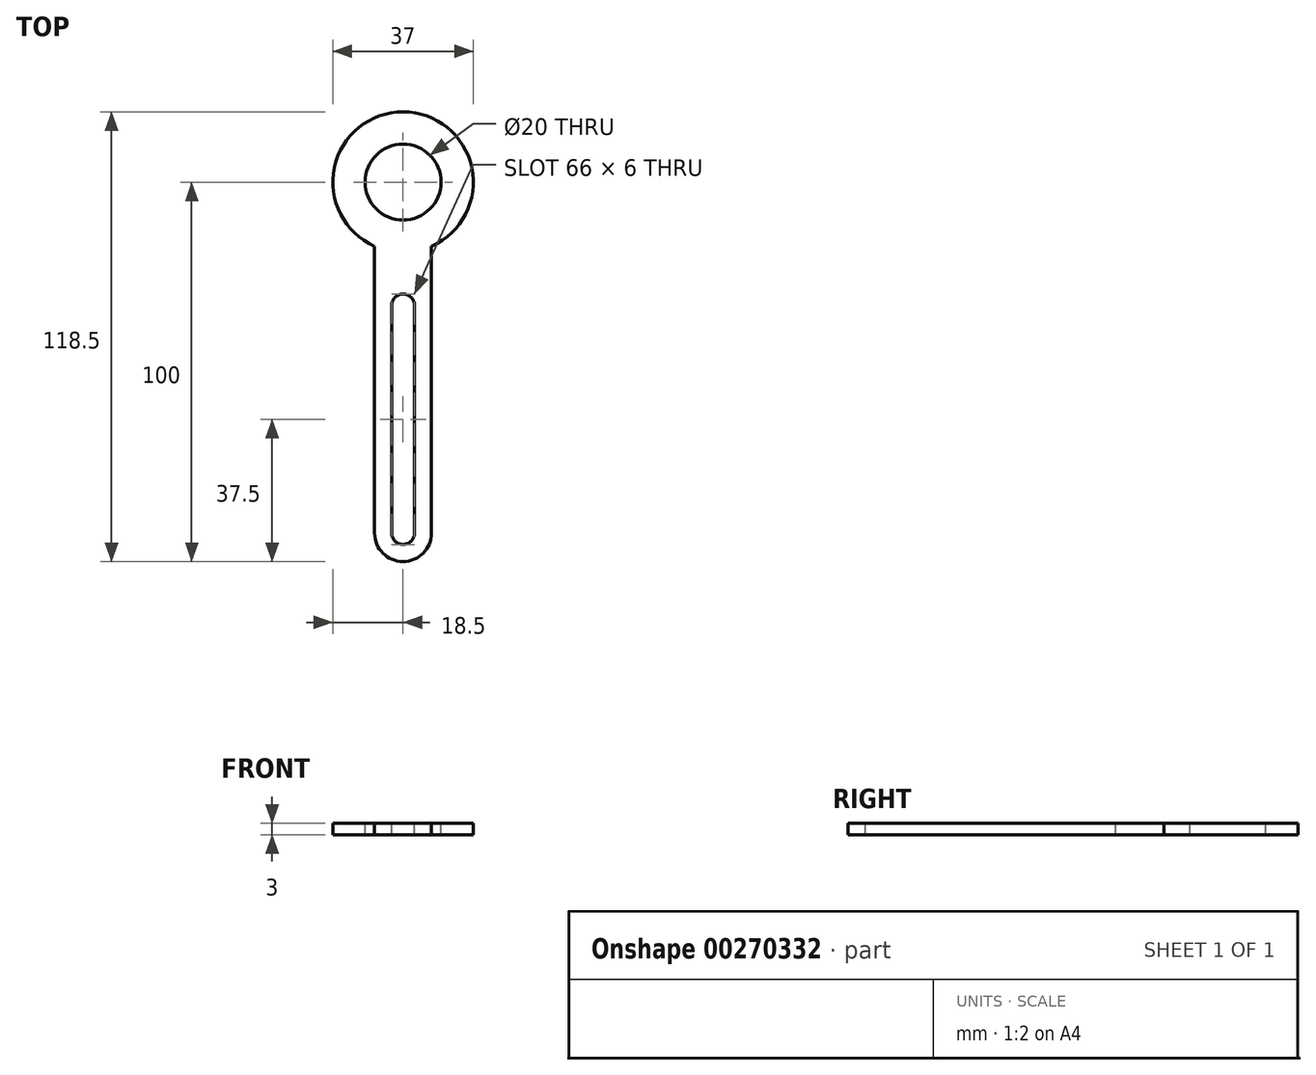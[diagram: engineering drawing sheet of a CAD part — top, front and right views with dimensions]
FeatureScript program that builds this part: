
annotation { "Feature Type Name" : "Feature", "Feature Type Description" : "" }
export const myFeature = defineFeature(function(context is Context, id is Id, definition is map)
    precondition{}
    {
        {
            var Q0;
            Q0=qCreatedBy(makeId("Top.planeOp"),FACE);
            var sketch = newSketch(context, id + "F0", { "sketchPlane" : qUnion([Q0])});
            skCircle(sketch, "E0", {"center": v(0, 0) * mm, "radius": 18.5 * mm});
            skLineSegment(sketch, "E1.bottom", {"start": v(7.5, -100) * mm, "end": v(-7.5, -100) * mm});
            skLineSegment(sketch, "E1.top", {"start": v(7.5, 100) * mm, "end": v(-7.5, 100) * mm});
            skLineSegment(sketch, "E1.left", {"start": v(7.5, -100) * mm, "end": v(7.5, 100) * mm});
            skLineSegment(sketch, "E1.right", {"start": v(-7.5, -100) * mm, "end": v(-7.5, 100) * mm});
            skSolve(sketch);
        }
        {
            var Q0;
            {var subQ0=sQuery(id+"F0.wireOp",EDGE,"E1.right");var subQ1=sQuery(id+"F0.wireOp",EDGE,"E0");var subQ2=makeQuery(id+"F0.imprint","INTERSECT",VERTEX,{"disambiguationData":[OD(0.0)],"derivedFrom":[subQ1,subQ0]});Q0=makeQuery(id+"F0.imprint","IMPRINT",FACE,{"disambiguationData":[TD([[makeQuery(id+"F0.imprint","IMPRINT",EDGE,{"disambiguationData":[TD([[subQ2,1.0]])],"derivedFrom":subQ1}),1.0]])]});}
            var Q1;
            {var subQ0=sQuery(id+"F0.wireOp",EDGE,"E1.right");var subQ1=sQuery(id+"F0.wireOp",EDGE,"E0");var subQ2=makeQuery(id+"F0.imprint","INTERSECT",VERTEX,{"disambiguationData":[OD(0.0)],"derivedFrom":[subQ1,subQ0]});Q1=makeQuery(id+"F0.imprint","IMPRINT",FACE,{"disambiguationData":[TD([[makeQuery(id+"F0.imprint","IMPRINT",EDGE,{"disambiguationData":[TD([[subQ2,-1.0]])],"derivedFrom":subQ1}),1.0]])]});}
            var Q2;
            {var subQ0=sQuery(id+"F0.wireOp",EDGE,"E1.left");var subQ1=sQuery(id+"F0.wireOp",EDGE,"E0");var subQ2=makeQuery(id+"F0.imprint","INTERSECT",VERTEX,{"disambiguationData":[OD(0.0)],"derivedFrom":[subQ1,subQ0]});Q2=makeQuery(id+"F0.imprint","IMPRINT",FACE,{"disambiguationData":[TD([[makeQuery(id+"F0.imprint","IMPRINT",EDGE,{"disambiguationData":[TD([[subQ2,1.0]])],"derivedFrom":subQ1}),1.0]])]});}
            var Q3;
            {var subQ5=sQuery(id+"F0.wireOp",EDGE,"E1.bottom");Q3=makeQuery(id+"F0.imprint","IMPRINT",FACE,{"disambiguationData":[TD([[makeQuery(id+"F0.imprint","IMPRINT",EDGE,{"derivedFrom":subQ5}),-1.0]])]});}
            extrude(context, id + "F1", {"entities" : qUnion([Q0, Q1, Q2, Q3]), "depth" : 3 * mm});
        }
        {
            var Q0;
            Q0=makeQuery(id+"F1.opExtrude","CAP_FACE",FACE,{"disambiguationData":[OSD([sQuery(id+"F0.wireOp",EDGE,"E0"),sQuery(id+"F0.wireOp",EDGE,"E1.bottom"),sQuery(id+"F0.wireOp",EDGE,"E1.left"),sQuery(id+"F0.wireOp",EDGE,"E1.right")])],"isStart":false});
            var sketch = newSketch(context, id + "F2", { "sketchPlane" : qUnion([Q0])});
            skCircle(sketch, "E2", {"center": v(0, 0) * mm, "radius": 10 * mm});
            skSolve(sketch);
        }
        {
            var Q0;
            Q0 = qSketchRegion(id + "F2", true);
            extrude(context, id + "F3", {"entities" : qUnion([Q0]), "operationType" : NewBodyOperationType.REMOVE, "oppositeDirection" : true, "depth" : 25 * mm});
        }
        {
            var Q0;
            Q0=makeQuery(id+"F1.opExtrude","SWEPT_EDGE",EDGE,{"disambiguationData":[OSD([sQuery(id+"F0.wireOp",EDGE,"E1.bottom"),sQuery(id+"F0.wireOp",EDGE,"E1.left")])]});
            var Q1;
            Q1=makeQuery(id+"F1.opExtrude","SWEPT_EDGE",EDGE,{"disambiguationData":[OSD([sQuery(id+"F0.wireOp",EDGE,"E1.bottom"),sQuery(id+"F0.wireOp",EDGE,"E1.right")])]});
            fillet(context, id + "F4", {"entities" : qUnion([Q0, Q1]), "radius" : 7.5 * mm, "tangentPropagation" : true, "allowEdgeOverflow" : false});
        }
        {
            var Q0;
            Q0=makeQuery(id+"F1.opExtrude","CAP_FACE",FACE,{"disambiguationData":[OSD([sQuery(id+"F0.wireOp",EDGE,"E0"),sQuery(id+"F0.wireOp",EDGE,"E1.bottom"),sQuery(id+"F0.wireOp",EDGE,"E1.left"),sQuery(id+"F0.wireOp",EDGE,"E1.right")])],"isStart":false});
            var sketch = newSketch(context, id + "F5", { "sketchPlane" : qUnion([Q0])});
            skLineSegment(sketch, "E3", {"start": v(0, -92.5) * mm, "end": v(0, -32.5) * mm});
            skArc(sketch, "E4.0.startCap", {"start": v(3, -92.5) * mm, "mid": v(0, -95.5) * mm, "end": v(-3, -92.5) * mm});
            skArc(sketch, "E4.0.endCap", {"start": v(-3, -32.5) * mm, "mid": v(0, -29.5) * mm, "end": v(3, -32.5) * mm});
            skLineSegment(sketch, "E4.0.left", {"start": v(-3, -92.5) * mm, "end": v(-3, -32.5) * mm});
            skLineSegment(sketch, "E4.0.right", {"start": v(3, -92.5) * mm, "end": v(3, -32.5) * mm});
            skSolve(sketch);
        }
        {
            var Q0;
            Q0 = qSketchRegion(id + "F5", true);
            extrude(context, id + "F6", {"entities" : qUnion([Q0]), "operationType" : NewBodyOperationType.REMOVE, "oppositeDirection" : true, "depth" : 25 * mm});
        }
    });
